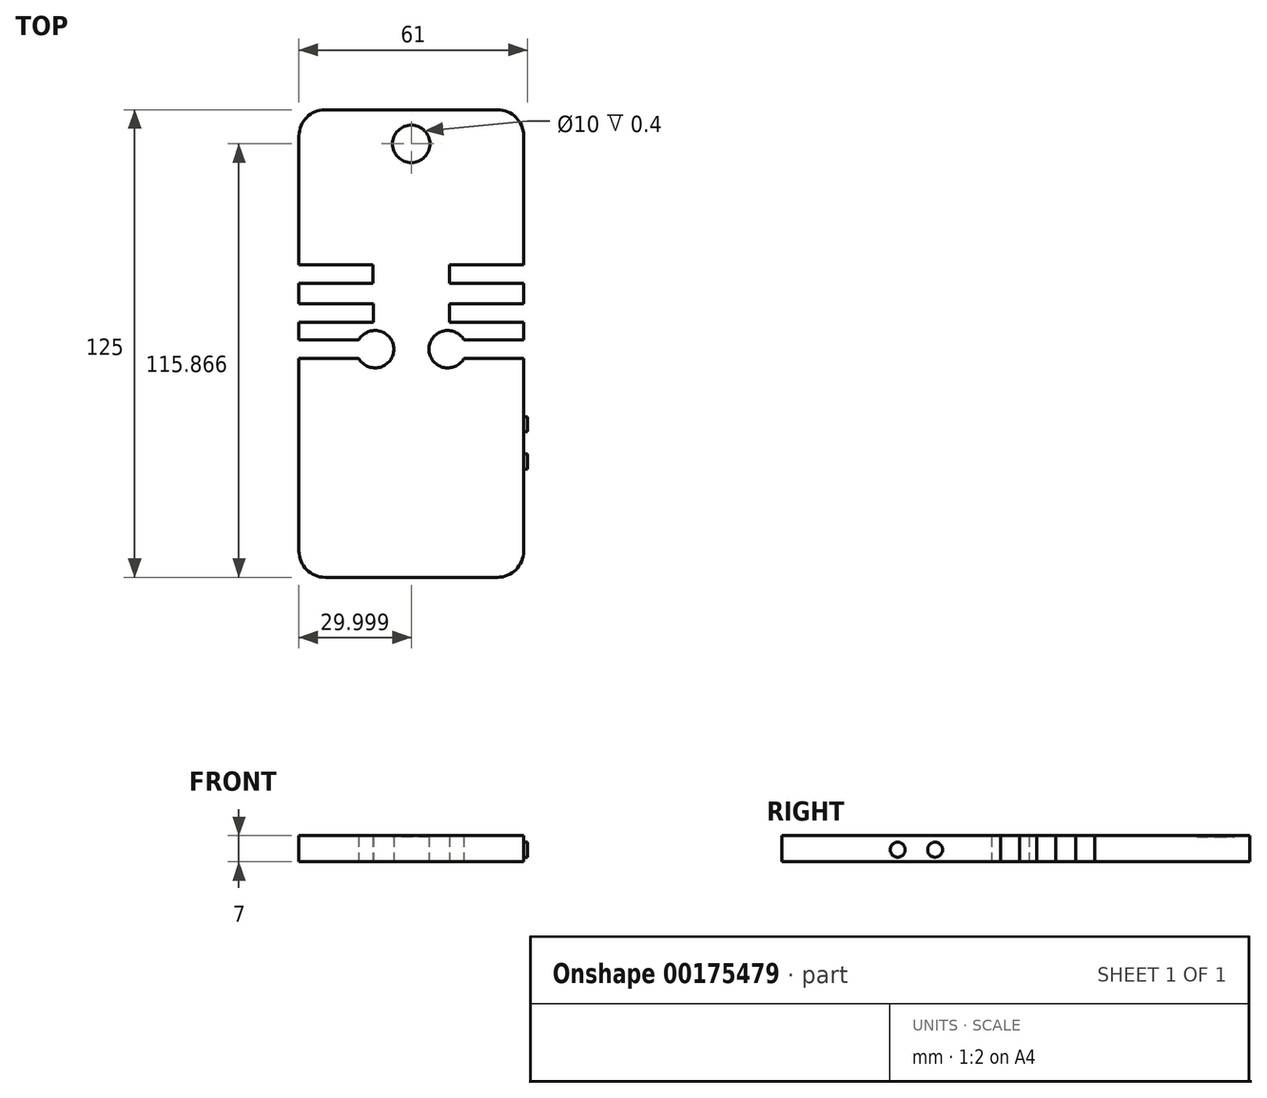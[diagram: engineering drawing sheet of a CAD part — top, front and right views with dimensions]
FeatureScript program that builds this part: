
annotation { "Feature Type Name" : "Feature", "Feature Type Description" : "" }
export const myFeature = defineFeature(function(context is Context, id is Id, definition is map)
    precondition{}
    {
        {
            var Q0;
            Q0=qCreatedBy(makeId("Top.planeOp"),FACE);
            var sketch = newSketch(context, id + "F0", { "sketchPlane" : qUnion([Q0])});
            skLineSegment(sketch, "E0.bottom", {"start": v(-25.2, 62.37) * mm, "end": v(34.8, 62.37) * mm});
            skLineSegment(sketch, "E0.top", {"start": v(-25.2, -62.63) * mm, "end": v(34.8, -62.63) * mm});
            skLineSegment(sketch, "E0.left", {"start": v(-25.2, 62.37) * mm, "end": v(-25.2, -62.63) * mm});
            skLineSegment(sketch, "E0.right", {"start": v(34.8, 62.37) * mm, "end": v(34.8, -62.63) * mm});
            skSolve(sketch);
        }
        {
            var Q0;
            Q0=makeQuery(id+"F0.imprint","IMPRINT",FACE,{"disambiguationData":[TD([[makeQuery(id+"F0.imprint","IMPRINT",EDGE,{"derivedFrom":sQuery(id+"F0.wireOp",EDGE,"E0.bottom")}),-1.0]])]});
            extrude(context, id + "F1", {"entities" : qUnion([Q0]), "depth" : 7 * mm});
        }
        {
            var Q0;
            Q0=makeQuery(id+"F1.opExtrude","SWEPT_EDGE",EDGE,{"disambiguationData":[OSD([sQuery(id+"F0.wireOp",EDGE,"E0.top"),sQuery(id+"F0.wireOp",EDGE,"E0.left")])]});
            fillet(context, id + "F2", {"entities" : qUnion([Q0]), "radius" : 7 * mm, "tangentPropagation" : true, "allowEdgeOverflow" : false});
        }
        {
            var Q0;
            Q0=makeQuery(id+"F1.opExtrude","SWEPT_EDGE",EDGE,{"disambiguationData":[OSD([sQuery(id+"F0.wireOp",EDGE,"E0.bottom"),sQuery(id+"F0.wireOp",EDGE,"E0.left")])]});
            var Q1;
            Q1=makeQuery(id+"F1.opExtrude","SWEPT_EDGE",EDGE,{"disambiguationData":[OSD([sQuery(id+"F0.wireOp",EDGE,"E0.top"),sQuery(id+"F0.wireOp",EDGE,"E0.right")])]});
            fillet(context, id + "F3", {"entities" : qUnion([Q0, Q1]), "radius" : 7 * mm, "tangentPropagation" : true, "allowEdgeOverflow" : false});
        }
        {
            var Q0;
            Q0=makeQuery(id+"F1.opExtrude","SWEPT_EDGE",EDGE,{"disambiguationData":[OSD([sQuery(id+"F0.wireOp",EDGE,"E0.bottom"),sQuery(id+"F0.wireOp",EDGE,"E0.right")])]});
            fillet(context, id + "F4", {"entities" : qUnion([Q0]), "radius" : 7 * mm, "tangentPropagation" : true, "allowEdgeOverflow" : false});
        }
        {
            var Q0;
            Q0=makeQuery(id+"F1.opExtrude","SWEPT_FACE",FACE,{"disambiguationData":[OSD([sQuery(id+"F0.wireOp",EDGE,"E0.right")])]});
            var sketch = newSketch(context, id + "F5", { "sketchPlane" : qUnion([Q0])});
            skCircle(sketch, "E1", {"center": v(-31.68, 3.22) * mm, "radius": 2 * mm});
            skCircle(sketch, "E2", {"center": v(-21.68, 3.22) * mm, "radius": 2 * mm});
            skLineSegment(sketch, "E3", {"start": v(-39.78, 3.22) * mm, "end": v(-45.78, 3.22) * mm});
            skLineSegment(sketch, "E4", {"start": v(-45.78, 3.4) * mm, "end": v(-45.78, 2.4) * mm});
            skLineSegment(sketch, "E5", {"start": v(-45.78, 2.4) * mm, "end": v(-41.56, 2.65) * mm});
            skLineSegment(sketch, "E6", {"start": v(-42.05, 1.9) * mm, "end": v(-49.6, -0.73) * mm});
            skSolve(sketch);
        }
        {
            var Q0;
            Q0=makeQuery(id+"F5.imprint","IMPRINT",FACE,{"disambiguationData":[TD([[makeQuery(id+"F5.imprint","IMPRINT",EDGE,{"derivedFrom":sQuery(id+"F5.wireOp",EDGE,"E1")}),1.0]])]});
            var Q1;
            Q1=makeQuery(id+"F5.imprint","IMPRINT",FACE,{"disambiguationData":[TD([[makeQuery(id+"F5.imprint","IMPRINT",EDGE,{"derivedFrom":sQuery(id+"F5.wireOp",EDGE,"E2")}),1.0]])]});
            extrude(context, id + "F6", {"entities" : qUnion([Q0, Q1]), "operationType" : NewBodyOperationType.ADD, "depth" : 1 * mm});
        }
        {
            var Q0;
            Q0=makeQuery(id+"F1.opExtrude","CAP_FACE",FACE,{"disambiguationData":[OSD([sQuery(id+"F0.wireOp",EDGE,"E0.bottom"),sQuery(id+"F0.wireOp",EDGE,"E0.top"),sQuery(id+"F0.wireOp",EDGE,"E0.left"),sQuery(id+"F0.wireOp",EDGE,"E0.right")])],"isStart":false});
            var sketch = newSketch(context, id + "F7", { "sketchPlane" : qUnion([Q0])});
            skLineSegment(sketch, "E7", {"start": v(34.8, 45.37) * mm, "end": v(-25.2, 45.37) * mm});
            skCircle(sketch, "E8", {"center": v(4.8, 53.24) * mm, "radius": 5 * mm});
            skSolve(sketch);
        }
        {
            var Q0;
            Q0=qCreatedBy(makeId("Top.planeOp"),FACE);
            var sketch = newSketch(context, id + "F8", { "sketchPlane" : qUnion([Q0])});
            skLineSegment(sketch, "E9", {"start": v(-22.53, -46.5) * mm, "end": v(32.03, -46.5) * mm});
            skPoint(sketch, "E10.startSnap0", {"position": v(4.75, -46.5) * mm});
            skLineSegment(sketch, "E11", {"start": v(5, -50.06) * mm, "end": v(9.58, -50.06) * mm});
            skLineSegment(sketch, "E12", {"start": v(5, -50.06) * mm, "end": v(0.19, -50.06) * mm});
            skLineSegment(sketch, "E13", {"start": v(5, -52.06) * mm, "end": v(0, -52.06) * mm});
            skLineSegment(sketch, "E14", {"start": v(5, -52.06) * mm, "end": v(9.77, -52.06) * mm});
            skArc(sketch, "E15", {"start": v(9.77, -52.06) * mm, "mid": v(10.19, -51.01) * mm, "end": v(9.58, -50.06) * mm});
            skArc(sketch, "E16", {"start": v(0.19, -50.06) * mm, "mid": v(-0.42, -51.01) * mm, "end": v(0, -52.06) * mm});
            skPoint(sketch, "E17.orphan", {"position": v(0, -50.06) * mm});
            skSolve(sketch);
        }
        {
            var Q0;
            Q0=qCreatedBy(makeId("Top.planeOp"),FACE);
            var sketch = newSketch(context, id + "F9", { "sketchPlane" : qUnion([Q0])});
            skLineSegment(sketch, "E18.bottom", {"start": v(-25.4, 20.91) * mm, "end": v(-5.4, 20.91) * mm});
            skLineSegment(sketch, "E18.top", {"start": v(-25.4, 15.91) * mm, "end": v(-5.4, 15.91) * mm});
            skLineSegment(sketch, "E18.left", {"start": v(-25.4, 20.91) * mm, "end": v(-25.4, 15.91) * mm});
            skLineSegment(sketch, "E18.right", {"start": v(-5.4, 20.91) * mm, "end": v(-5.4, 15.91) * mm});
            skLineSegment(sketch, "E19.bottom", {"start": v(34.96, 20.91) * mm, "end": v(14.96, 20.91) * mm});
            skLineSegment(sketch, "E19.top", {"start": v(34.96, 15.91) * mm, "end": v(14.96, 15.91) * mm});
            skLineSegment(sketch, "E19.left", {"start": v(34.96, 20.91) * mm, "end": v(34.96, 15.91) * mm});
            skLineSegment(sketch, "E19.right", {"start": v(14.96, 20.91) * mm, "end": v(14.96, 15.91) * mm});
            skLineSegment(sketch, "E20.bottom", {"start": v(-25.34, 10.5) * mm, "end": v(-5.34, 10.5) * mm});
            skLineSegment(sketch, "E20.top", {"start": v(-25.34, 5.5) * mm, "end": v(-5.34, 5.5) * mm});
            skLineSegment(sketch, "E20.left", {"start": v(-25.34, 10.5) * mm, "end": v(-25.34, 5.5) * mm});
            skLineSegment(sketch, "E20.right", {"start": v(-5.34, 10.5) * mm, "end": v(-5.34, 5.5) * mm});
            skLineSegment(sketch, "E21.bottom", {"start": v(34.94, 10.5) * mm, "end": v(14.94, 10.5) * mm});
            skLineSegment(sketch, "E21.top", {"start": v(34.94, 5.5) * mm, "end": v(14.94, 5.5) * mm});
            skLineSegment(sketch, "E21.left", {"start": v(34.94, 10.5) * mm, "end": v(34.94, 5.5) * mm});
            skLineSegment(sketch, "E21.right", {"start": v(14.94, 10.5) * mm, "end": v(14.94, 5.5) * mm});
            skLineSegment(sketch, "E22.bottom", {"start": v(-25.98, 0.86) * mm, "end": v(-9.2, 0.86) * mm});
            skLineSegment(sketch, "E22.top", {"start": v(-25.98, -4.14) * mm, "end": v(-9.2, -4.14) * mm});
            skLineSegment(sketch, "E22.left", {"start": v(-25.98, 0.86) * mm, "end": v(-25.98, -4.14) * mm});
            skLineSegment(sketch, "E23.bottom", {"start": v(36.63, 0.86) * mm, "end": v(18.85, 0.86) * mm});
            skLineSegment(sketch, "E23.top", {"start": v(36.63, -4.14) * mm, "end": v(18.85, -4.14) * mm});
            skLineSegment(sketch, "E23.left", {"start": v(36.63, 0.86) * mm, "end": v(36.63, -4.14) * mm});
            skCircle(sketch, "E24", {"center": v(-4.88, -1.64) * mm, "radius": 5 * mm});
            skArc(sketch, "E25", {"start": v(18.85, 0.86) * mm, "mid": v(9.52, -1.64) * mm, "end": v(18.85, -4.14) * mm});
            skPoint(sketch, "E26.orphan", {"position": v(14.52, 0.86) * mm});
            skPoint(sketch, "E23.right.end.orphan", {"position": v(14.52, -4.14) * mm});
            skPoint(sketch, "E27.orphan", {"position": v(-4.88, -4.14) * mm});
            skPoint(sketch, "E28.orphan", {"position": v(-4.88, 0.86) * mm});
            skSolve(sketch);
        }
        {
            var Q0;
            Q0 = qSketchRegion(id + "F9", true);
            extrude(context, id + "F10", {"entities" : qUnion([Q0]), "operationType" : NewBodyOperationType.REMOVE, "depth" : 88.1 * mm});
        }
        {
            var Q0;
            Q0=sQuery(id+"F8.wireOp",EDGE,"E9");
            extrude(context, id + "F11", {"bodyType" : ToolBodyType.SURFACE, "surfaceEntities" : qUnion([Q0]), "depth" : 7 * mm});
        }
        {
            var Q0;
            Q0=makeQuery(id+"F7.imprint","IMPRINT",FACE,{"disambiguationData":[TD([[makeQuery(id+"F7.imprint","IMPRINT",EDGE,{"derivedFrom":sQuery(id+"F7.wireOp",EDGE,"E8")}),1.0]])]});
            extrude(context, id + "F12", {"entities" : qUnion([Q0]), "operationType" : NewBodyOperationType.REMOVE, "oppositeDirection" : true, "depth" : 0.4 * mm});
        }
    });
